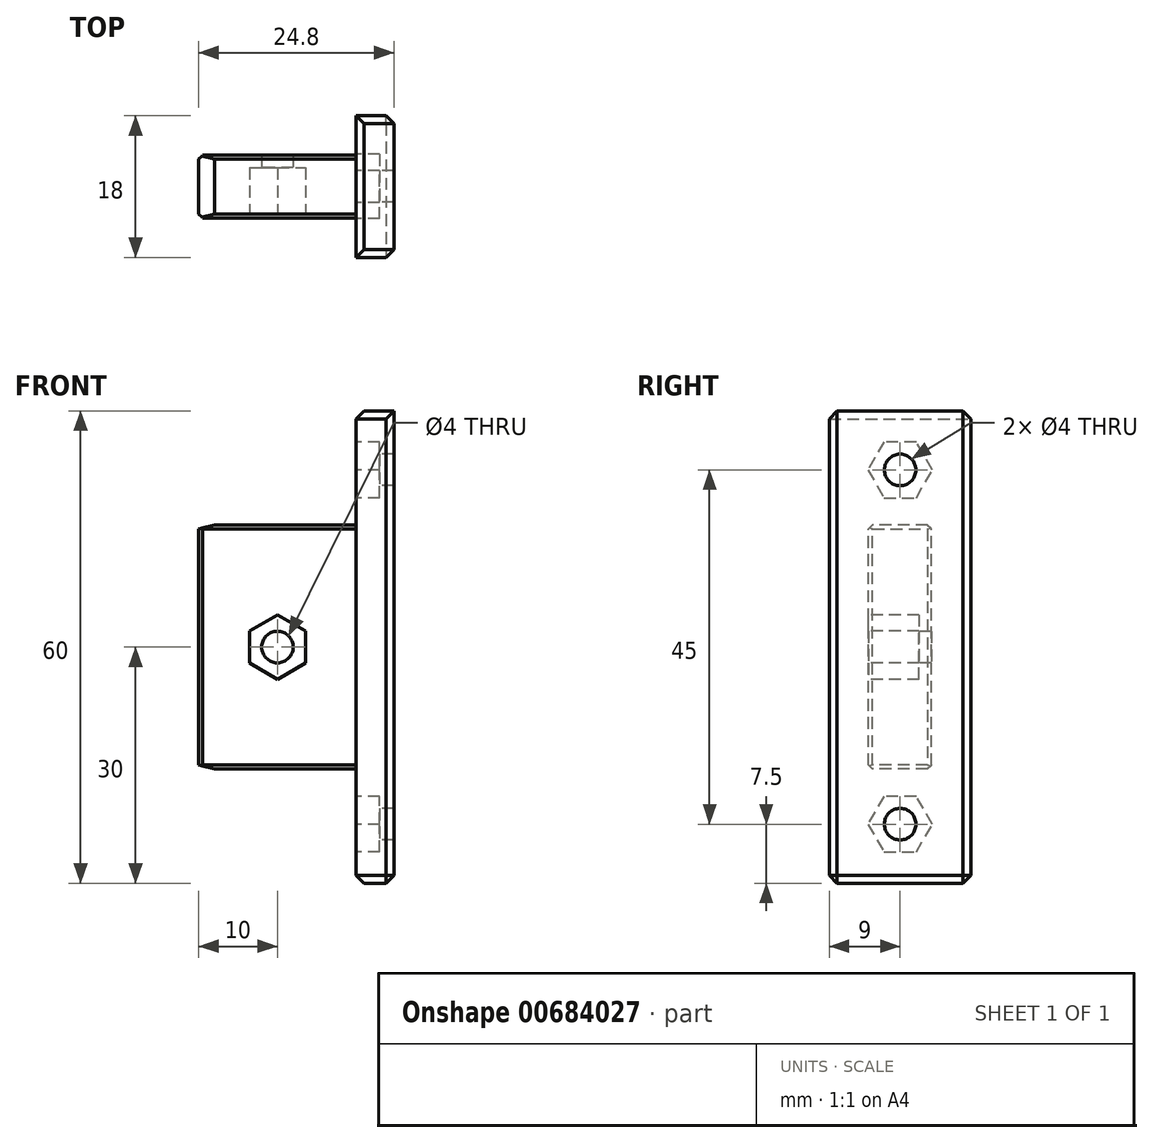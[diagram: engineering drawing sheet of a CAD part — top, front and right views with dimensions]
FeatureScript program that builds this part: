
annotation { "Feature Type Name" : "Feature", "Feature Type Description" : "" }
export const myFeature = defineFeature(function(context is Context, id is Id, definition is map)
    precondition{}
    {
        {
            var Q0;
            Q0=qCreatedBy(makeId("Right.planeOp"),FACE);
            var sketch = newSketch(context, id + "F0", { "sketchPlane" : qUnion([Q0])});
            skLineSegment(sketch, "E0.bottom", {"start": v(0, 0) * mm, "end": v(-8, 0) * mm});
            skLineSegment(sketch, "E0.top", {"start": v(0, 31) * mm, "end": v(-8, 31) * mm});
            skLineSegment(sketch, "E0.left", {"start": v(0, 0) * mm, "end": v(0, 31) * mm});
            skLineSegment(sketch, "E0.right", {"start": v(-8, 0) * mm, "end": v(-8, 31) * mm});
            skSolve(sketch);
        }
        {
            var Q0;
            Q0 = qSketchRegion(id + "F0", true);
            extrude(context, id + "F1", {"entities" : qUnion([Q0]), "oppositeDirection" : true, "depth" : 20 * mm, "offsetDistance" : 25 * mm});
        }
        {
            var Q0;
            Q0=makeQuery(id+"F1.opExtrude","SWEPT_FACE",FACE,{"disambiguationData":[OSD([sQuery(id+"F0.wireOp",EDGE,"E0.right")])]});
            var sketch = newSketch(context, id + "F2", { "sketchPlane" : qUnion([Q0])});
            skPoint(sketch, "E1", {"position": v(0, 15.5) * mm});
            skLineSegment(sketch, "E2", {"start": v(0, 15.5) * mm, "end": v(-20, 15.5) * mm, "construction": true});
            skCircle(sketch, "E3.cCircle", {"center": v(-10, 15.5) * mm, "radius": 3.55 * mm, "construction": true});
            skLineSegment(sketch, "E3.0", {"start": v(-6.45, 17.55) * mm, "end": v(-6.45, 13.45) * mm});
            skLineSegment(sketch, "E3.1", {"start": v(-6.45, 13.45) * mm, "end": v(-10, 11.4) * mm});
            skLineSegment(sketch, "E3.2", {"start": v(-10, 11.4) * mm, "end": v(-13.55, 13.45) * mm});
            skLineSegment(sketch, "E3.3", {"start": v(-13.55, 13.45) * mm, "end": v(-13.55, 17.55) * mm});
            skLineSegment(sketch, "E3.4", {"start": v(-13.55, 17.55) * mm, "end": v(-10, 19.6) * mm});
            skLineSegment(sketch, "E3.5", {"start": v(-10, 19.6) * mm, "end": v(-6.45, 17.55) * mm});
            skPoint(sketch, "E3.0.midPoint", {"position": v(-6.45, 15.5) * mm});
            skSolve(sketch);
        }
        {
            var Q0;
            Q0=makeQuery(id+"F2.imprint","IMPRINT",FACE,{"disambiguationData":[TD([[makeQuery(id+"F2.imprint","IMPRINT",EDGE,{"derivedFrom":sQuery(id+"F2.wireOp",EDGE,"E3.0")}),-1.0]])]});
            var Q1;
            Q1 = qConstructionFilter(qBodyType(qCreatedBy(id + "F2" ,EDGE), BodyType.WIRE), ConstructionObject.NO);
            extrude(context, id + "F3", {"entities" : qUnion([Q0]), "operationType" : NewBodyOperationType.REMOVE, "surfaceEntities" : qUnion([Q1]), "oppositeDirection" : true, "depth" : (8 - 0.4 * 4) * mm, "offsetDistance" : 25 * mm});
        }
        {
            var Q0;
            Q0=makeQuery(id+"F3.boolean.opBoolean","COPY",FACE,{"derivedFrom":makeQuery(id+"F3.opExtrude","CAP_FACE",FACE,{"disambiguationData":[OSD([sQuery(id+"F2.wireOp",EDGE,"E3.0"),sQuery(id+"F2.wireOp",EDGE,"E3.1"),sQuery(id+"F2.wireOp",EDGE,"E3.2"),sQuery(id+"F2.wireOp",EDGE,"E3.3"),sQuery(id+"F2.wireOp",EDGE,"E3.4"),sQuery(id+"F2.wireOp",EDGE,"E3.5")])],"isStart":false})});
            var sketch = newSketch(context, id + "F4", { "sketchPlane" : qUnion([Q0])});
            skPoint(sketch, "E4.0", {"position": v(-10, 15.5) * mm});
            skCircle(sketch, "E5", {"center": v(-10, 15.5) * mm, "radius": 2 * mm});
            skSolve(sketch);
        }
        {
            var Q0;
            Q0 = qSketchRegion(id + "F4", true);
            extrude(context, id + "F5", {"entities" : qUnion([Q0]), "operationType" : NewBodyOperationType.REMOVE, "endBound" : BoundingType.THROUGH_ALL, "oppositeDirection" : true, "depth" : 25 * mm, "offsetDistance" : 25 * mm});
        }
        {
            var Q0;
            Q0=makeQuery(id+"F1.opExtrude","CAP_EDGE",EDGE,{"disambiguationData":[OSD([sQuery(id+"F0.wireOp",EDGE,"E0.left")])],"isStart":true});
            cPoint(context, id + "F6", {"entities" : qUnion([Q0]), "parameter" : 0.5});
        }
        {
            var Q0;
            Q0=sQuery(id+"F2.wireOp",EDGE,"E2");
            cPoint(context, id + "F7", {"entities" : qUnion([Q0]), "parameter" : 0.5});
        }
        {
            var Q0;
            Q0 = qCreatedBy(id + "F6" ,VERTEX);
            var Q1;
            Q1=sQuery(id+"F2.wireOp",VERTEX,"E1");
            var Q2;
            Q2 = qCreatedBy(id + "F7" ,VERTEX);
            cPlane(context, id + "F8", {"entities" : qUnion([Q0, Q1, Q2]), "cplaneType" : CPlaneType.THREE_POINT, "offset" : 25 * mm, "width" : 150 * mm, "height" : 150 * mm});
        }
        {
            var Q0;
            Q0=qCreatedBy(id+"F8.planeOp",FACE);
            var sketch = newSketch(context, id + "F9", { "sketchPlane" : qUnion([Q0])});
            skLineSegment(sketch, "E6.bottom", {"start": v(0, -13) * mm, "end": v(4.8, -13) * mm});
            skLineSegment(sketch, "E6.top", {"start": v(0, 5) * mm, "end": v(4.8, 5) * mm});
            skLineSegment(sketch, "E6.left", {"start": v(0, -13) * mm, "end": v(0, 5) * mm});
            skLineSegment(sketch, "E6.right", {"start": v(4.8, -13) * mm, "end": v(4.8, 5) * mm});
            skPoint(sketch, "E7", {"position": v(0, -4) * mm});
            skSolve(sketch);
        }
        {
            var Q0;
            Q0=makeQuery(id+"F9.imprint","IMPRINT",FACE,{"disambiguationData":[TD([[makeQuery(id+"F9.imprint","IMPRINT",EDGE,{"derivedFrom":sQuery(id+"F9.wireOp",EDGE,"E6.bottom")}),1.0]])]});
            extrude(context, id + "F10", {"entities" : qUnion([Q0]), "operationType" : NewBodyOperationType.ADD, "endBound" : BoundingType.SYMMETRIC, "depth" : 60 * mm, "offsetDistance" : 25 * mm});
        }
        {
            var Q0;
            Q0=makeQuery(id+"F10.opExtrude","SWEPT_FACE",FACE,{"disambiguationData":[OSD([sQuery(id+"F9.wireOp",EDGE,"E6.left")])]});
            var sketch = newSketch(context, id + "F11", { "sketchPlane" : qUnion([Q0])});
            skCircle(sketch, "E8.cCircle", {"center": v(4, 38) * mm, "radius": 3.55 * mm, "construction": true});
            skPoint(sketch, "E8.cCircle.centerSnap0", {"position": v(4, 31) * mm});
            skLineSegment(sketch, "E8.0", {"start": v(1.95, 41.55) * mm, "end": v(6.05, 41.55) * mm});
            skLineSegment(sketch, "E8.1", {"start": v(6.05, 41.55) * mm, "end": v(8.1, 38) * mm});
            skLineSegment(sketch, "E8.2", {"start": v(8.1, 38) * mm, "end": v(6.05, 34.45) * mm});
            skLineSegment(sketch, "E8.3", {"start": v(6.05, 34.45) * mm, "end": v(1.95, 34.45) * mm});
            skLineSegment(sketch, "E8.4", {"start": v(1.95, 34.45) * mm, "end": v(-0.1, 38) * mm});
            skLineSegment(sketch, "E8.5", {"start": v(-0.1, 38) * mm, "end": v(1.95, 41.55) * mm});
            skPoint(sketch, "E8.0.midPoint", {"position": v(4, 41.55) * mm});
            skLineSegment(sketch, "E9", {"start": v(13, 15.5) * mm, "end": v(-5, 15.5) * mm, "construction": true});
            skCircle(sketch, "E10.cCircle", {"center": v(4, -7) * mm, "radius": 3.55 * mm, "construction": true});
            skPoint(sketch, "E10.cCircle.centerSnap0", {"position": v(4, 0) * mm});
            skLineSegment(sketch, "E10.0", {"start": v(1.95, -3.45) * mm, "end": v(6.05, -3.45) * mm});
            skLineSegment(sketch, "E10.1", {"start": v(6.05, -3.45) * mm, "end": v(8.1, -7) * mm});
            skLineSegment(sketch, "E10.2", {"start": v(8.1, -7) * mm, "end": v(6.05, -10.55) * mm});
            skLineSegment(sketch, "E10.3", {"start": v(6.05, -10.55) * mm, "end": v(1.95, -10.55) * mm});
            skLineSegment(sketch, "E10.4", {"start": v(1.95, -10.55) * mm, "end": v(-0.1, -7) * mm});
            skLineSegment(sketch, "E10.5", {"start": v(-0.1, -7) * mm, "end": v(1.95, -3.45) * mm});
            skPoint(sketch, "E10.0.midPoint", {"position": v(4, -3.45) * mm});
            skSolve(sketch);
        }
        {
            var Q0;
            Q0 = qSketchRegion(id + "F11", true);
            extrude(context, id + "F12", {"entities" : qUnion([Q0]), "operationType" : NewBodyOperationType.REMOVE, "oppositeDirection" : true, "depth" : 3 * mm, "offsetDistance" : 25 * mm});
        }
        {
            var Q0;
            Q0=makeQuery(id+"F12.boolean.opBoolean","COPY",FACE,{"derivedFrom":makeQuery(id+"F12.opExtrude","CAP_FACE",FACE,{"disambiguationData":[OSD([sQuery(id+"F11.wireOp",EDGE,"E8.0"),sQuery(id+"F11.wireOp",EDGE,"E8.1"),sQuery(id+"F11.wireOp",EDGE,"E8.2"),sQuery(id+"F11.wireOp",EDGE,"E8.3"),sQuery(id+"F11.wireOp",EDGE,"E8.4"),sQuery(id+"F11.wireOp",EDGE,"E8.5")])],"isStart":false})});
            var sketch = newSketch(context, id + "F13", { "sketchPlane" : qUnion([Q0])});
            skPoint(sketch, "E11.0", {"position": v(4, 38) * mm});
            skPoint(sketch, "E12.0", {"position": v(4, -7) * mm});
            skCircle(sketch, "E13", {"center": v(4, 38) * mm, "radius": 2 * mm});
            skCircle(sketch, "E14", {"center": v(4, -7) * mm, "radius": 2 * mm});
            skSolve(sketch);
        }
        {
            var Q0;
            Q0 = qSketchRegion(id + "F13", true);
            extrude(context, id + "F14", {"entities" : qUnion([Q0]), "operationType" : NewBodyOperationType.REMOVE, "endBound" : BoundingType.THROUGH_ALL, "oppositeDirection" : true, "depth" : 25 * mm, "offsetDistance" : 25 * mm});
        }
        {
            var Q0;
            Q0=makeQuery(id+"F1.opExtrude","SWEPT_EDGE",EDGE,{"disambiguationData":[OSD([sQuery(id+"F0.wireOp",EDGE,"E0.top"),sQuery(id+"F0.wireOp",EDGE,"E0.right")])]});
            var Q1;
            Q1=makeQuery(id+"F1.opExtrude","SWEPT_EDGE",EDGE,{"disambiguationData":[OSD([sQuery(id+"F0.wireOp",EDGE,"E0.top"),sQuery(id+"F0.wireOp",EDGE,"E0.left")])]});
            var Q2;
            Q2=makeQuery(id+"F1.opExtrude","SWEPT_EDGE",EDGE,{"disambiguationData":[OSD([sQuery(id+"F0.wireOp",EDGE,"E0.bottom"),sQuery(id+"F0.wireOp",EDGE,"E0.left")])]});
            var Q3;
            Q3=makeQuery(id+"F1.opExtrude","SWEPT_EDGE",EDGE,{"disambiguationData":[OSD([sQuery(id+"F0.wireOp",EDGE,"E0.bottom"),sQuery(id+"F0.wireOp",EDGE,"E0.right")])]});
            var Q4;
            Q4=makeQuery(id+"F1.opExtrude","CAP_EDGE",EDGE,{"disambiguationData":[OSD([sQuery(id+"F0.wireOp",EDGE,"E0.right")])],"isStart":false});
            var Q5;
            Q5=makeQuery(id+"F1.opExtrude","CAP_EDGE",EDGE,{"disambiguationData":[OSD([sQuery(id+"F0.wireOp",EDGE,"E0.left")])],"isStart":false});
            chamfer(context, id + "F15", {"entities" : qUnion([Q0, Q1, Q2, Q3, Q4, Q5]), "width" : 0.5 * mm, "tangentPropagation" : true});
        }
        {
            var Q0;
            Q0=makeQuery(id+"F1.opExtrude","CAP_EDGE",EDGE,{"disambiguationData":[OSD([sQuery(id+"F0.wireOp",EDGE,"E0.top")])],"isStart":false});
            var Q1;
            Q1=makeQuery(id+"F1.opExtrude","CAP_EDGE",EDGE,{"disambiguationData":[OSD([sQuery(id+"F0.wireOp",EDGE,"E0.bottom")])],"isStart":false});
            chamfer(context, id + "F16", {"entities" : qUnion([Q0, Q1]), "chamferType" : ChamferType.TWO_OFFSETS, "width1" : 0.5 * mm, "oppositeDirection" : true, "width2" : 2 * mm, "tangentPropagation" : true});
        }
        {
            var Q0;
            Q0=makeQuery(id+"F10.opExtrude","CAP_EDGE",EDGE,{"disambiguationData":[OSD([sQuery(id+"F9.wireOp",EDGE,"E6.bottom")])],"isStart":false});
            var Q1;
            Q1=makeQuery(id+"F10.opExtrude","CAP_EDGE",EDGE,{"disambiguationData":[OSD([sQuery(id+"F9.wireOp",EDGE,"E6.top")])],"isStart":false});
            var Q2;
            Q2=makeQuery(id+"F10.opExtrude","CAP_EDGE",EDGE,{"disambiguationData":[OSD([sQuery(id+"F9.wireOp",EDGE,"E6.bottom")])],"isStart":true});
            var Q3;
            Q3=makeQuery(id+"F10.opExtrude","CAP_EDGE",EDGE,{"disambiguationData":[OSD([sQuery(id+"F9.wireOp",EDGE,"E6.top")])],"isStart":true});
            var Q4;
            Q4=makeQuery(id+"F10.opExtrude","SWEPT_EDGE",EDGE,{"disambiguationData":[OSD([sQuery(id+"F9.wireOp",EDGE,"E6.top"),sQuery(id+"F9.wireOp",EDGE,"E6.right")])]});
            var Q5;
            Q5=makeQuery(id+"F10.opExtrude","CAP_EDGE",EDGE,{"disambiguationData":[OSD([sQuery(id+"F9.wireOp",EDGE,"E6.right")])],"isStart":true});
            var Q6;
            Q6=makeQuery(id+"F10.opExtrude","SWEPT_EDGE",EDGE,{"disambiguationData":[OSD([sQuery(id+"F9.wireOp",EDGE,"E6.bottom"),sQuery(id+"F9.wireOp",EDGE,"E6.right")])]});
            var Q7;
            Q7=makeQuery(id+"F10.opExtrude","CAP_EDGE",EDGE,{"disambiguationData":[OSD([sQuery(id+"F9.wireOp",EDGE,"E6.left")])],"isStart":false});
            var Q8;
            Q8=makeQuery(id+"F10.opExtrude","CAP_EDGE",EDGE,{"disambiguationData":[OSD([sQuery(id+"F9.wireOp",EDGE,"E6.left")])],"isStart":true});
            chamfer(context, id + "F17", {"entities" : qUnion([Q0, Q1, Q2, Q3, Q4, Q5, Q6, Q7, Q8]), "width" : 1 * mm, "tangentPropagation" : true});
        }
    });
